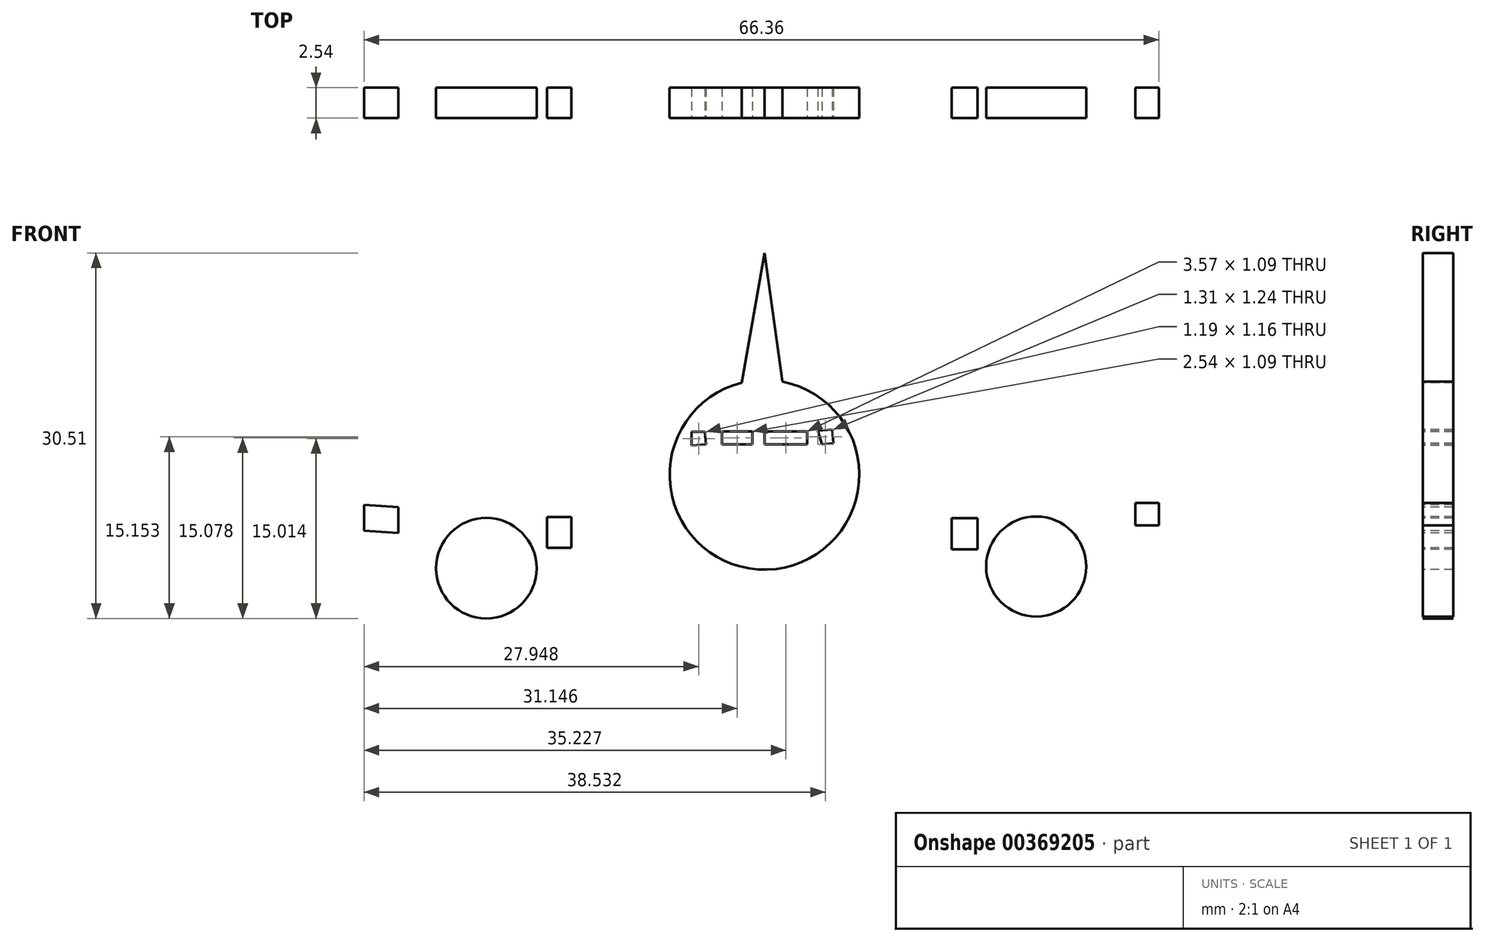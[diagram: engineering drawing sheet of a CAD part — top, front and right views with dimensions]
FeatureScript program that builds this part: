
annotation { "Feature Type Name" : "Feature", "Feature Type Description" : "" }
export const myFeature = defineFeature(function(context is Context, id is Id, definition is map)
    precondition{}
    {
        {
            var Q0;
            Q0=qCreatedBy(makeId("Front.planeOp"),FACE);
            var sketch = newSketch(context, id + "F0", { "sketchPlane" : qUnion([Q0])});
            skLineSegment(sketch, "E0", {"start": v(-7.9, -1.16) * mm, "end": v(-54.5, 1.96) * mm});
            skLineSegment(sketch, "E1", {"start": v(-6.65, -3.2) * mm, "end": v(-54.5, 0) * mm});
            skLineSegment(sketch, "E2", {"start": v(7.59, -1.46) * mm, "end": v(55.35, 2.52) * mm});
            skLineSegment(sketch, "E3", {"start": v(6.6, -3.27) * mm, "end": v(55.35, 0.8) * mm});
            skLineSegment(sketch, "E4", {"start": v(-6.65, -3.2) * mm, "end": v(-7.9, -1.16) * mm});
            skLineSegment(sketch, "E5", {"start": v(6.6, -3.27) * mm, "end": v(7.59, -1.46) * mm});
            skLineSegment(sketch, "E6", {"start": v(-7.68, 3.8) * mm, "end": v(-20.3, 5.48) * mm});
            skLineSegment(sketch, "E7", {"start": v(7.28, 3.8) * mm, "end": v(20.1, 5.4) * mm});
            skLineSegment(sketch, "E8", {"start": v(-7.4, 5.4) * mm, "end": v(-20.3, 5.48) * mm});
            skLineSegment(sketch, "E9", {"start": v(7, 5.4) * mm, "end": v(20.1, 5.4) * mm});
            skCircle(sketch, "E10", {"center": v(-23.22, -6.7) * mm, "radius": 4.2 * mm});
            skCircle(sketch, "E11", {"center": v(22.68, -6.55) * mm, "radius": 4.18 * mm});
            skCircle(sketch, "E12", {"center": v(0, 1.1) * mm, "radius": 7.92 * mm});
            skLineSegment(sketch, "E13", {"start": v(-1.9, 8.8) * mm, "end": v(0, 19.62) * mm});
            skLineSegment(sketch, "E14", {"start": v(1.5, 8.88) * mm, "end": v(0, 19.62) * mm});
            skLineSegment(sketch, "E15.bottom", {"start": v(3.57, 3.64) * mm, "end": v(0, 3.64) * mm});
            skLineSegment(sketch, "E15.top", {"start": v(3.57, 4.73) * mm, "end": v(0, 4.73) * mm});
            skLineSegment(sketch, "E15.left", {"start": v(3.57, 3.64) * mm, "end": v(3.57, 4.73) * mm});
            skLineSegment(sketch, "E15.right", {"start": v(0, 3.64) * mm, "end": v(0, 4.73) * mm});
            skLineSegment(sketch, "E16.bottom", {"start": v(-3.56, 3.64) * mm, "end": v(-1.02, 3.64) * mm});
            skLineSegment(sketch, "E16.top", {"start": v(-3.56, 4.73) * mm, "end": v(-1.02, 4.73) * mm});
            skLineSegment(sketch, "E16.left", {"start": v(-3.56, 3.64) * mm, "end": v(-3.56, 4.73) * mm});
            skLineSegment(sketch, "E16.right", {"start": v(-1.02, 3.64) * mm, "end": v(-1.02, 4.73) * mm});
            skLineSegment(sketch, "E17", {"start": v(5.75, 3.72) * mm, "end": v(5.65, 4.88) * mm});
            skLineSegment(sketch, "E18", {"start": v(5.75, 3.72) * mm, "end": v(4.78, 3.64) * mm});
            skLineSegment(sketch, "E19", {"start": v(5.65, 4.88) * mm, "end": v(4.44, 4.78) * mm});
            skLineSegment(sketch, "E20", {"start": v(4.44, 4.78) * mm, "end": v(4.78, 3.64) * mm});
            skLineSegment(sketch, "E21", {"start": v(-4.9, 3.64) * mm, "end": v(-6.09, 3.54) * mm});
            skLineSegment(sketch, "E22", {"start": v(-4.9, 3.64) * mm, "end": v(-4.99, 4.7) * mm});
            skLineSegment(sketch, "E23", {"start": v(-6.09, 3.54) * mm, "end": v(-6.09, 4.7) * mm});
            skLineSegment(sketch, "E24", {"start": v(-4.99, 4.7) * mm, "end": v(-6.09, 4.7) * mm});
            skLineSegment(sketch, "E25", {"start": v(-30.58, -1.6) * mm, "end": v(-30.58, -3.74) * mm});
            skLineSegment(sketch, "E26", {"start": v(-30.58, -3.74) * mm, "end": v(-33.44, -3.55) * mm});
            skLineSegment(sketch, "E27", {"start": v(-33.44, -3.55) * mm, "end": v(-33.44, -1.4) * mm});
            skLineSegment(sketch, "E28.bottom", {"start": v(15.63, -2.52) * mm, "end": v(17.79, -2.52) * mm});
            skLineSegment(sketch, "E28.top", {"start": v(15.63, -5.13) * mm, "end": v(17.79, -5.13) * mm});
            skLineSegment(sketch, "E28.left", {"start": v(15.63, -2.52) * mm, "end": v(15.63, -5.13) * mm});
            skLineSegment(sketch, "E28.right", {"start": v(17.79, -2.52) * mm, "end": v(17.79, -5.13) * mm});
            skLineSegment(sketch, "E29.bottom", {"start": v(-18.15, -2.43) * mm, "end": v(-16.11, -2.43) * mm});
            skLineSegment(sketch, "E29.top", {"start": v(-18.15, -5) * mm, "end": v(-16.11, -5) * mm});
            skLineSegment(sketch, "E29.left", {"start": v(-18.15, -2.43) * mm, "end": v(-18.15, -5) * mm});
            skLineSegment(sketch, "E29.right", {"start": v(-16.11, -2.43) * mm, "end": v(-16.11, -5) * mm});
            skLineSegment(sketch, "E30.bottom", {"start": v(30.98, -1.24) * mm, "end": v(32.92, -1.24) * mm});
            skLineSegment(sketch, "E30.top", {"start": v(30.98, -3.12) * mm, "end": v(32.92, -3.12) * mm});
            skLineSegment(sketch, "E30.left", {"start": v(30.98, -1.24) * mm, "end": v(30.98, -3.12) * mm});
            skLineSegment(sketch, "E30.right", {"start": v(32.92, -1.24) * mm, "end": v(32.92, -3.12) * mm});
            skLineSegment(sketch, "E31", {"start": v(55.35, 0.8) * mm, "end": v(55.44, 2.52) * mm});
            skLineSegment(sketch, "E32", {"start": v(-54.5, 0) * mm, "end": v(-54.6, 1.96) * mm});
            skSolve(sketch);
        }
        {
            var Q0;
            Q0 = qSketchRegion(id + "F0", true);
            extrude(context, id + "F1", {"entities" : qUnion([Q0]), "oppositeDirection" : true, "depth" : 2.54 * mm});
        }
    });
